# Revit family: Gleiter radial-axial GL-200 o.Lasche, 2xAG
name_source: partatom
category: HLS-Bauteile
revit_build: Autodesk Revit 2017 (Build: 20190507_1515(x64)
units: mm (PartAtom-declared; Revit-internal decimal feet)

## family parameters
Arbeitsebenenbasiert = Ja
Beim Laden mit Abzugskörper schneiden = Nein
Bemaßung runder Anschluss = Durchmesser verwenden
Gemeinsam genutzt = Ja
Immer vertikal = Nein
Raumberechnungspunkt = Nein
Teiletyp = Normal

## types (4) — shared parameters
B = 250 mm  [stored 0.82021 ft]
B1 = 58 mm  [stored 0.190289 ft]
Breite = 90 mm  [stored 0.295276 ft]
Fabrikat = MEFA
Gleitreibungsfaktor = 0.15 - 0.25
H1 = 15 mm  [stored 0.0492126 ft]
H2 = 21 mm  [stored 0.0688976 ft]
Haftreibungsfaktor = 0,2 - 0,3
Kurztext1 = Gleitelement radial-axial GL 200
L1 = 80 mm  [stored 0.262467 ft]
Länge = 250 mm  [stored 0.82021 ft]
MD = 3 mm  [stored 0.00984252 ft]
Material Gleitstreifen = Kunststoff
Materialname Gleitstreifen = Polyamid 6
Mengeneinheit = St
Vorgabe-Ansicht = 1219 mm
max. Temperaturbeständigkeit = 100 °C
vpe = 1 St

## per-type parameters (varying)
| type | A | Anschlussgewinde | Artikelnummer | EAN | Gewicht | Gewicht pro Bauteil | H | Kurztext2 |
| Gleiter ra-ax GL-200, 2x M10 | 150 mm | 6kt-Mutter parametrik : Hutmutter gedreht M10 (4130010) | 077047101 | 4250928417626 | 0.90 kg | 0.90 kg | 42 mm  [stored 0.137795 ft] | Anschluss 2 x M10 ohne Lasche |
| Gleiter ra-ax GL-200, 2x M12 | 150 mm | 6kt-Mutter parametrik : Hutmutter gedreht M12 (4130012) | 077047001 | 4250928417602 | 0.92 kg | 0.92 kg | 44 mm  [stored 0.144357 ft] | Anschluss 2 x M12 ohne Lasche |
| Gleiter ra-ax GL-200, 2x M16 | 160 mm  [stored 0.524934 ft] | 6kt-Mutter parametrik : Mutter M16 (4120522) | 077047201 | 4250928417640 | 0.95 kg | 0.95 kg | 43 mm  [stored 0.141076 ft] | Anschluss 2 x M16 ohne Lasche |
| Gleiter ra-ax GL-200, 2x 1/2" | 160 mm  [stored 0.524934 ft] | Runde Gewindeanschlusse parametrik : Muffe 1/2´´ (0009865) | 077047301 | 4250928417664 | 0.93 kg | 0.93 kg | 43 mm  [stored 0.141076 ft] | Anschluss 2 x 1/2'' ohne Lasche |

note: [stored X ft] marks values corroborated as IEEE doubles in the binary element streams (Revit-internal decimal feet)

## geometry (parser evidence)
native form markers: Sweep x3
no freeform markers — native parametric forms only
